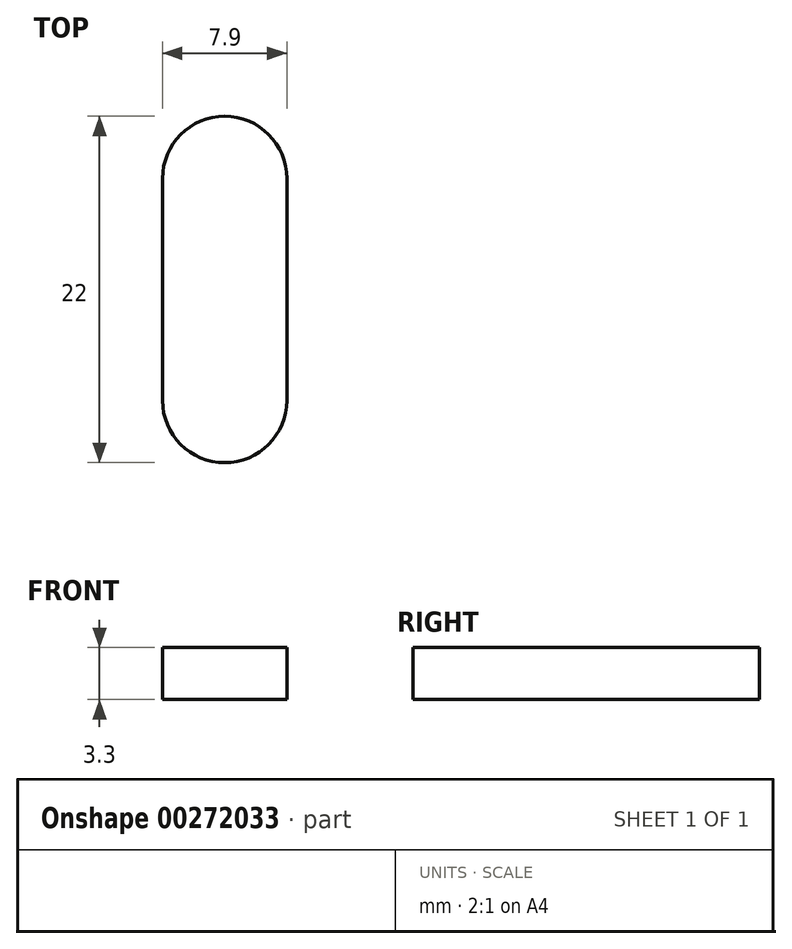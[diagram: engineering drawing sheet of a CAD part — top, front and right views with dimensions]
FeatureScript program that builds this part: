
annotation { "Feature Type Name" : "Feature", "Feature Type Description" : "" }
export const myFeature = defineFeature(function(context is Context, id is Id, definition is map)
    precondition{}
    {
        {
            var Q0;
            Q0=qCreatedBy(makeId("Top.planeOp"),FACE);
            var sketch = newSketch(context, id + "F0", { "sketchPlane" : qUnion([Q0])});
            skLineSegment(sketch, "E0", {"start": v(-3.95, 0) * mm, "end": v(-3.95, -14.1) * mm});
            skLineSegment(sketch, "E1", {"start": v(3.95, 0) * mm, "end": v(3.95, -14.1) * mm});
            skArc(sketch, "E2", {"start": v(3.95, 0) * mm, "mid": v(0, 3.95) * mm, "end": v(-3.95, 0) * mm});
            skArc(sketch, "E3", {"start": v(-3.95, -14.1) * mm, "mid": v(0, -18.05) * mm, "end": v(3.95, -14.1) * mm});
            skSolve(sketch);
        }
        {
            var Q0;
            Q0=makeQuery(id+"F0.imprint","IMPRINT",FACE,{"disambiguationData":[TD([[makeQuery(id+"F0.imprint","IMPRINT",EDGE,{"derivedFrom":sQuery(id+"F0.wireOp",EDGE,"E0")}),1.0]])]});
            extrude(context, id + "F1", {"entities" : qUnion([Q0]), "depth" : 3.3 * mm});
        }
    });
